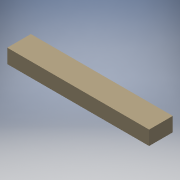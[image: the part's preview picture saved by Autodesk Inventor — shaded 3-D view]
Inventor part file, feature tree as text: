
AUTODESK INVENTOR PART (.ipt)
format: ipt  version: 2016 (Build 200138000, 138)  size: 87,552 bytes
history: native  units: in
note: dims shown in document units (in); Inventor stores cm internally (conversion verified against a paired STEP export)
features: extrude x1, sketch x1
ambient origin geometry x8: Origin, YZ Plane, XZ Plane, XY Plane, X Axis, Y Axis, Z Axis, Center Point
bodies: Solid1 (feature_tree)
feature tree (2):
  extrude  "Extrusion1"  Depth=1.5in
  sketch  "Sketch1"  dims[d0=0.75in d1=1.5in d2=15.0in d3=0.0in]
